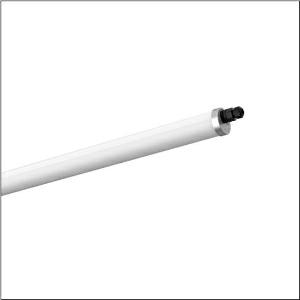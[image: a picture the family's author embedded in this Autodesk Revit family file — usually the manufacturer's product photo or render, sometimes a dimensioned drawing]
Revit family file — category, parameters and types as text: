
# Revit family: monsun_r__31_tube_51ft107n480a_b45d
name_source: partatom
category: Lighting Fixtures
units: mm (PartAtom-declared; Revit-internal decimal feet)

## family parameters
Cut with Voids When Loaded = No
Host = Face
Light Source = No
Part Type = Normal
Room Calculation Point = No
Round Connector Dimension = Use Diameter
Shared = No

## types (1)
- Monsun® 31 Tube (1 x LED, 8000 lm, 50 W, 4000K)
    Apparent Load = 50 VA
    CIE Flux Codes = 42 71 89 91 100
    Color Rendering = 80
    Color Temperature = 4000K
    Default Elevation = 1800 mm
    Description = Monsun® 31 Tube, tubular luminaire, primary optical cover: diffuser, of PMMA, light emission: direct distribution, primary light characteristic: symmetric, installation type: suspended mounting, surface-mounted, LED, rated luminous flux: 8.000lm, luminous efficacy: 160lm/W, light colour: 840, colour temperature: 4000K, with with 1 terminal, 3-pole, max. 2.5mm², through-wiring: 3x 1.5mm², mains connection: 220..240V, AC, 50/60Hz, rated input power: 50W, housing, cylindrical, of PMMA, semi-transparent, matt white, with luminaire and ceiling fastening, V4A, mounting with brackets of stainless steel, length: 1.560mm, diameter: 75mm, end cap, of stainless steel (V4A), protection rating (complete): IP67/IP69K, insulation class (complete): insulation class I (protective earthing), certification: CE, UKCA, impact resistance: IK07, permissible operating ambient temperature: -20..+40°C, corresponds to IFS (International Featured Standards) requirements for safety and quality in the food industry, usage in unprotected outdoor area possible with horizontal mounting, contact your sales advisor before using the luminaires in applications with unclear chemical exposure, large temperature fluctuations or condensation-forming humidity, packaging unit: 1 piece
    Height = 83 mm
    Lamp = 1 x LED
    Lamp Light Flux = 8000 lm
    Lamp Power = 50 W
    Lamp count = 1
    Length = 1560 mm
    Luminous efficacy = 160 lm/W
    Manufacturer = Siteco
    ModVariant = No
    Model = 51FT107N480A
    Mounting Place = Ceiling
    Mounting Type = Pendant
    Number of Poles = 1
    OnlyDefault = Yes
    Power Factor = 1
    Product Name = Monsun® 31 Tube
    Product group = tubular luminaire
    ProductGroupID = 906
    Protection Class = Protection class I
    RLX_Detail_Level = 1
    RLX_Emergency_Light_Flux = 0 lm
    RLX_Emergency_Type = 0
    RLX_Emergency_Type_DB = No
    RlxData = <blob elided: 25321 chars, md5=e25d555c>
    Socket = socket
    Standby Power = 0 W
    System Light Flux = 8000 lm
    System Power = 50 W
    Type Comments = Product without accessories
    Type Image = l_1228461.jpg
    URL = http://relux.com
    VarID = ---
    Voltage = 0 V
    Weight = 0.00 kg
    Width = 75 mm

## geometry (parser evidence)
native form markers: Blend x4, Sweep x12
no freeform markers — native parametric forms only
